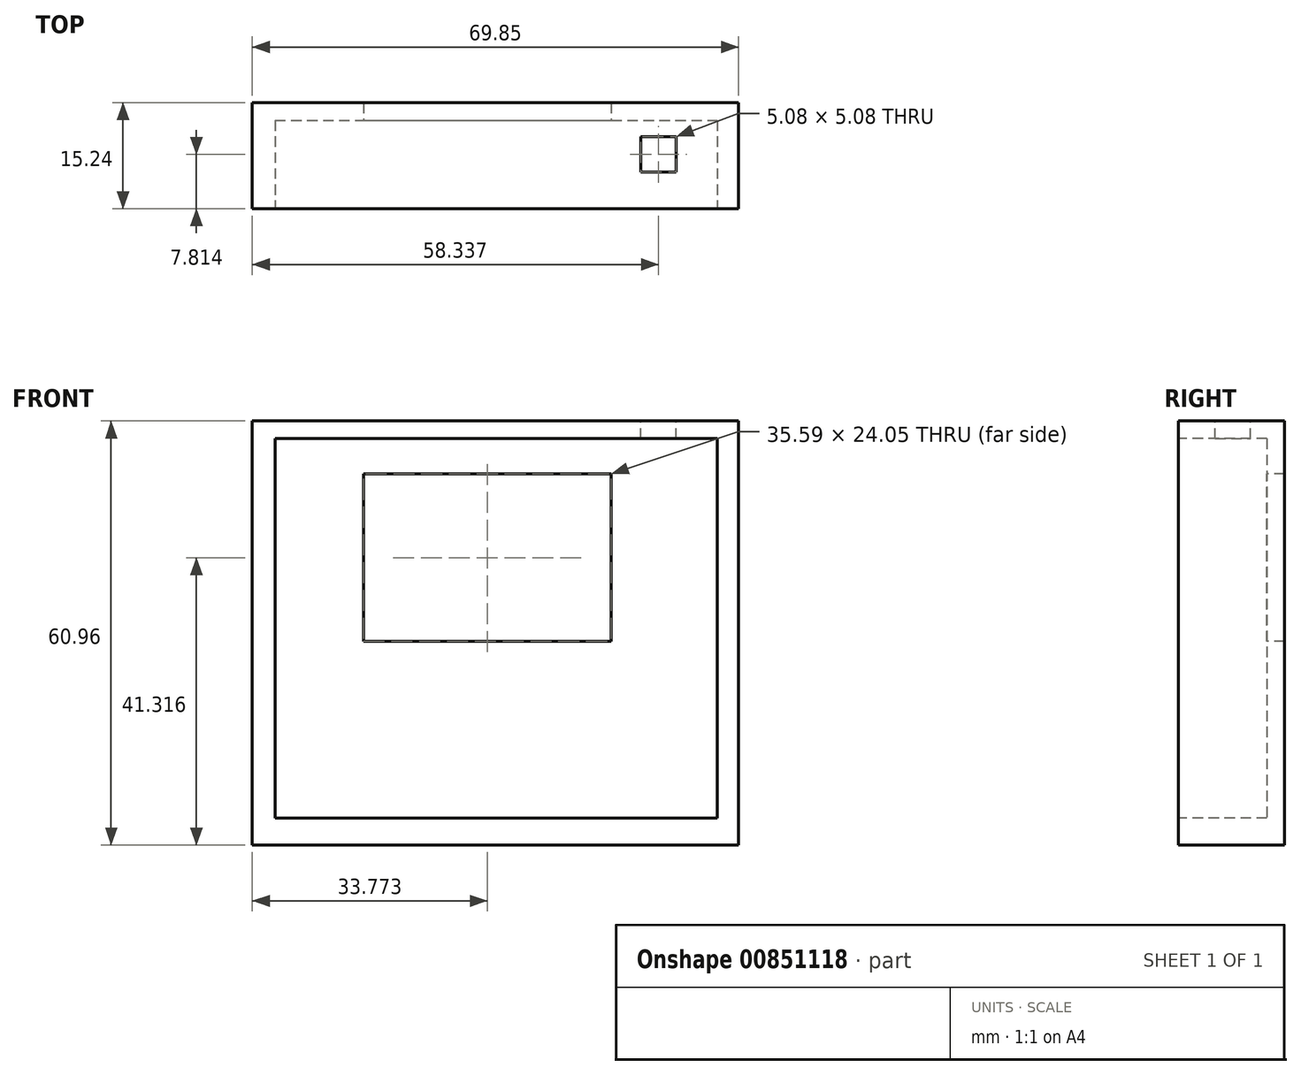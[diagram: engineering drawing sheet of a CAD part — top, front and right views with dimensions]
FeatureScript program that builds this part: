
annotation { "Feature Type Name" : "Feature", "Feature Type Description" : "" }
export const myFeature = defineFeature(function(context is Context, id is Id, definition is map)
    precondition{}
    {
        {
            var Q0;
            Q0=qCreatedBy(makeId("Front.planeOp"),FACE);
            var sketch = newSketch(context, id + "F0", { "sketchPlane" : qUnion([Q0])});
            skLineSegment(sketch, "E0.bottom", {"start": v(-25.73, 11.23) * mm, "end": v(44.12, 11.23) * mm});
            skLineSegment(sketch, "E0.top", {"start": v(-25.73, -49.73) * mm, "end": v(44.12, -49.73) * mm});
            skLineSegment(sketch, "E0.left", {"start": v(-25.73, 11.23) * mm, "end": v(-25.73, -49.73) * mm});
            skLineSegment(sketch, "E0.right", {"start": v(44.12, 11.23) * mm, "end": v(44.12, -49.73) * mm});
            skSolve(sketch);
        }
        {
            var Q0;
            Q0 = qSketchRegion(id + "F0", true);
            extrude(context, id + "F1", {"entities" : qUnion([Q0]), "depth" : 15.24 * mm, "offsetDistance" : 25.4 * mm});
        }
        {
            var Q0;
            Q0=makeQuery(id+"F1.opExtrude","CAP_FACE",FACE,{"disambiguationData":[OSD([sQuery(id+"F0.wireOp",EDGE,"E0.bottom"),sQuery(id+"F0.wireOp",EDGE,"E0.top"),sQuery(id+"F0.wireOp",EDGE,"E0.left"),sQuery(id+"F0.wireOp",EDGE,"E0.right")])],"isStart":false});
            var sketch = newSketch(context, id + "F2", { "sketchPlane" : qUnion([Q0])});
            skLineSegment(sketch, "E1.bottom", {"start": v(-22.45, 8.7) * mm, "end": v(41.05, 8.7) * mm});
            skLineSegment(sketch, "E1.top", {"start": v(-22.45, -45.84) * mm, "end": v(41.05, -45.84) * mm});
            skLineSegment(sketch, "E1.left", {"start": v(-22.45, 8.7) * mm, "end": v(-22.45, -45.84) * mm});
            skLineSegment(sketch, "E1.right", {"start": v(41.05, 8.7) * mm, "end": v(41.05, -45.84) * mm});
            skSolve(sketch);
        }
        {
            var Q0;
            Q0 = qSketchRegion(id + "F2", true);
            extrude(context, id + "F3", {"entities" : qUnion([Q0]), "operationType" : NewBodyOperationType.REMOVE, "oppositeDirection" : true, "depth" : 12.7 * mm, "offsetDistance" : 25.4 * mm});
        }
        {
            var Q0;
            Q0=makeQuery(id+"FYbiorAiRuS0CZO_1.boolean.opBoolean","MERGE",FACE,{"derivedFrom":[makeQuery(id+"F1.opExtrude","SWEPT_FACE",FACE,{"disambiguationData":[OSD([sQuery(id+"F0.wireOp",EDGE,"E0.bottom")])]}),makeQuery(id+"FYbiorAiRuS0CZO_1.opExtrude","SWEPT_FACE",FACE,{"disambiguationData":[OSD([sQuery(id+"FpbL8GRrL8R4aOa_1.wireOp",EDGE,"bqimuS8e-3krb-Lw13-xGXX-q1oaJWy3KEm0.bottom")])]}),makeQuery(id+"FYbiorAiRuS0CZO_1.opExtrude","SWEPT_FACE",FACE,{"disambiguationData":[OSD([sQuery(id+"FpbL8GRrL8R4aOa_1.wireOp",EDGE,"bc04618b-a9f7-4e9e-9518-1ea45e8db5690.MirrorCS")])]})]});
            var sketch = newSketch(context, id + "F4", { "sketchPlane" : qUnion([Q0])});
            skLineSegment(sketch, "E2.bottom", {"start": v(30.07, -4.89) * mm, "end": v(35.15, -4.89) * mm});
            skLineSegment(sketch, "E2.top", {"start": v(30.07, -9.97) * mm, "end": v(35.15, -9.97) * mm});
            skLineSegment(sketch, "E2.left", {"start": v(30.07, -4.89) * mm, "end": v(30.07, -9.97) * mm});
            skLineSegment(sketch, "E2.right", {"start": v(35.15, -4.89) * mm, "end": v(35.15, -9.97) * mm});
            skSolve(sketch);
        }
        {
            var Q0;
            Q0 = qSketchRegion(id + "F4", true);
            extrude(context, id + "F5", {"entities" : qUnion([Q0]), "operationType" : NewBodyOperationType.REMOVE, "oppositeDirection" : true, "depth" : 25.4 * mm, "offsetDistance" : 25.4 * mm});
        }
        {
            var Q0;
            Q0=makeQuery(id+"F3.boolean.opBoolean","COPY",FACE,{"derivedFrom":makeQuery(id+"F3.opExtrude","CAP_FACE",FACE,{"disambiguationData":[OSD([sQuery(id+"F2.wireOp",EDGE,"E1.bottom"),sQuery(id+"F2.wireOp",EDGE,"E1.top"),sQuery(id+"F2.wireOp",EDGE,"E1.left"),sQuery(id+"F2.wireOp",EDGE,"E1.right")])],"isStart":false})});
            var sketch = newSketch(context, id + "F6", { "sketchPlane" : qUnion([Q0])});
            skLineSegment(sketch, "E3", {"start": v(-9.75, -11.76) * mm, "end": v(-9.75, -20.44) * mm});
            skLineSegment(sketch, "E4", {"start": v(-9.75, -20.44) * mm, "end": v(25.84, -20.44) * mm});
            skLineSegment(sketch, "E5", {"start": v(25.84, -20.44) * mm, "end": v(25.84, 3.61) * mm});
            skLineSegment(sketch, "E6", {"start": v(25.84, 3.61) * mm, "end": v(9.3, 3.61) * mm});
            skLineSegment(sketch, "E7", {"start": v(-9.75, 3.61) * mm, "end": v(9.3, 3.61) * mm});
            skLineSegment(sketch, "E8", {"start": v(-9.75, -11.76) * mm, "end": v(-9.75, 3.61) * mm});
            skSolve(sketch);
        }
        {
            var Q0;
            Q0 = qSketchRegion(id + "F6", true);
            extrude(context, id + "F7", {"entities" : qUnion([Q0]), "operationType" : NewBodyOperationType.REMOVE, "oppositeDirection" : true, "depth" : 25.4 * mm, "offsetDistance" : 25.4 * mm});
        }
    });
